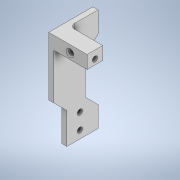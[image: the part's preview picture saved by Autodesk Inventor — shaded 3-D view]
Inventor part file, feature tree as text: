
AUTODESK INVENTOR PART (.ipt)
format: ipt  version: 2021 (Build 250183000, 183)  size: 185,856 bytes
history: native  units: mm
features: sketch x8, extrude x5, hole x3, chamfer x2, fillet x1
ambient origin geometry x8: Origin, YZ Plane, XZ Plane, XY Plane, X Axis, Y Axis, Z Axis, Center Point
bodies: Solid1 (feature_tree)
feature tree (19):
  extrude  "Extrusion1"  Depth=5.0mm
  hole  "Hole1"  [1 undecoded]
  hole  "Hole2"  [1 undecoded]
  extrude  "Extrusion2"  Depth=17.0mm
  hole  "Hole3"  [1 undecoded]
  extrude  "Extrusion3"  Depth=2.0mm
  extrude  "Extrusion4"  Depth=10.0mm
  chamfer  "Chamfer1"  Distance=10.0mm
  fillet  "Fillet1"  Radius=2.0mm
  extrude  "Extrusion5"  Depth=2.0mm TaperAngle=0.0deg
  chamfer  "Chamfer2"  Distance=5.0mm
  sketch  "Sketch1"  dims[d0=12.0mm d1=5.0mm]
  sketch  "Sketch2"  dims[d2=6.0mm d3=0.0mm d4=5.8mm]
  sketch  "Sketch3"  dims[d5=2.8mm]
  sketch  "Sketch4"  dims[d6=2.0mm d7=6.0mm d8=3.0mm d9=2.0mm d10=90.0deg d11=5.0mm d12=20.594885mm d13=3.0mm]
  sketch  "Sketch5"  dims[d14=3.0mm]
  sketch  "Sketch6"  dims[d15=2.0mm d16=6.0mm d17=3.0mm d18=2.0mm d19=90.0deg d20=3.0mm d21=20.594885mm d22=17.0mm]
  sketch  "Sketch7"  dims[d23=39.6mm d24=2.0mm d25=0.0mm]
  sketch  "Sketch8"  dims[d26=3.0mm d27=9.0mm d28=10.0mm d29=10.0mm d30=2.0mm d31=6.0mm d32=4.0mm d33=2.0mm d34=90.0deg d35=3.0mm d36=20.594885mm d37=2.0mm d38=0.8mm d39=0.0mm d40=5.0mm d41=8.0mm d42=8.0mm d43=2.0mm d44=0.0mm d45=5.0mm d46=2.0mm d47=45.0deg d48=2.0mm d49=5.0mm d50=12.0mm d51=10.0mm d52=0.0mm d53=5.0mm d54=2.0mm d55=45.0deg]
note: 3 required parameter values undecoded (feature->parameter linkage not recoverable at this tier; creation-order binding heuristic only, values carry confidence <= 0.55)
